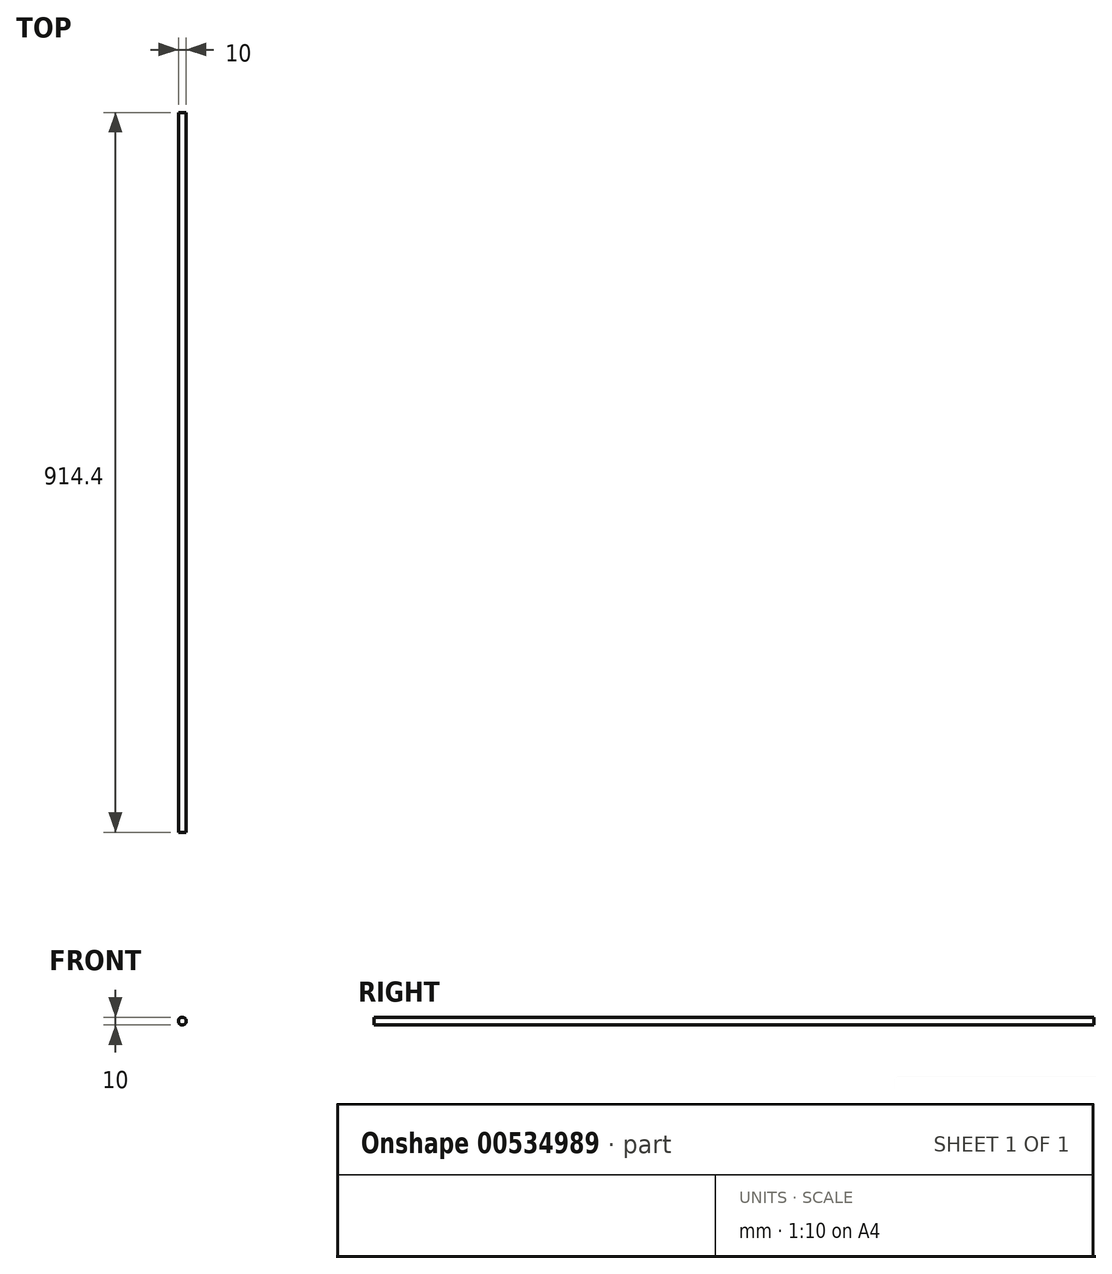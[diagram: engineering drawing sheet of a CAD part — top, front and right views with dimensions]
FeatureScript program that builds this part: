
annotation { "Feature Type Name" : "Feature", "Feature Type Description" : "" }
export const myFeature = defineFeature(function(context is Context, id is Id, definition is map)
    precondition{}
    {
        {
            var Q0;
            Q0=qCreatedBy(makeId("Front.planeOp"),FACE);
            var sketch = newSketch(context, id + "F0", { "sketchPlane" : qUnion([Q0])});
            skCircle(sketch, "E0", {"center": v(0, 0) * mm, "radius": 5 * mm});
            skSolve(sketch);
        }
        {
            var Q0;
            Q0 = qSketchRegion(id + "F0", true);
            extrude(context, id + "F1", {"entities" : qUnion([Q0]), "depth" : 914.4 * mm, "offsetDistance" : 25.4 * mm});
        }
    });
